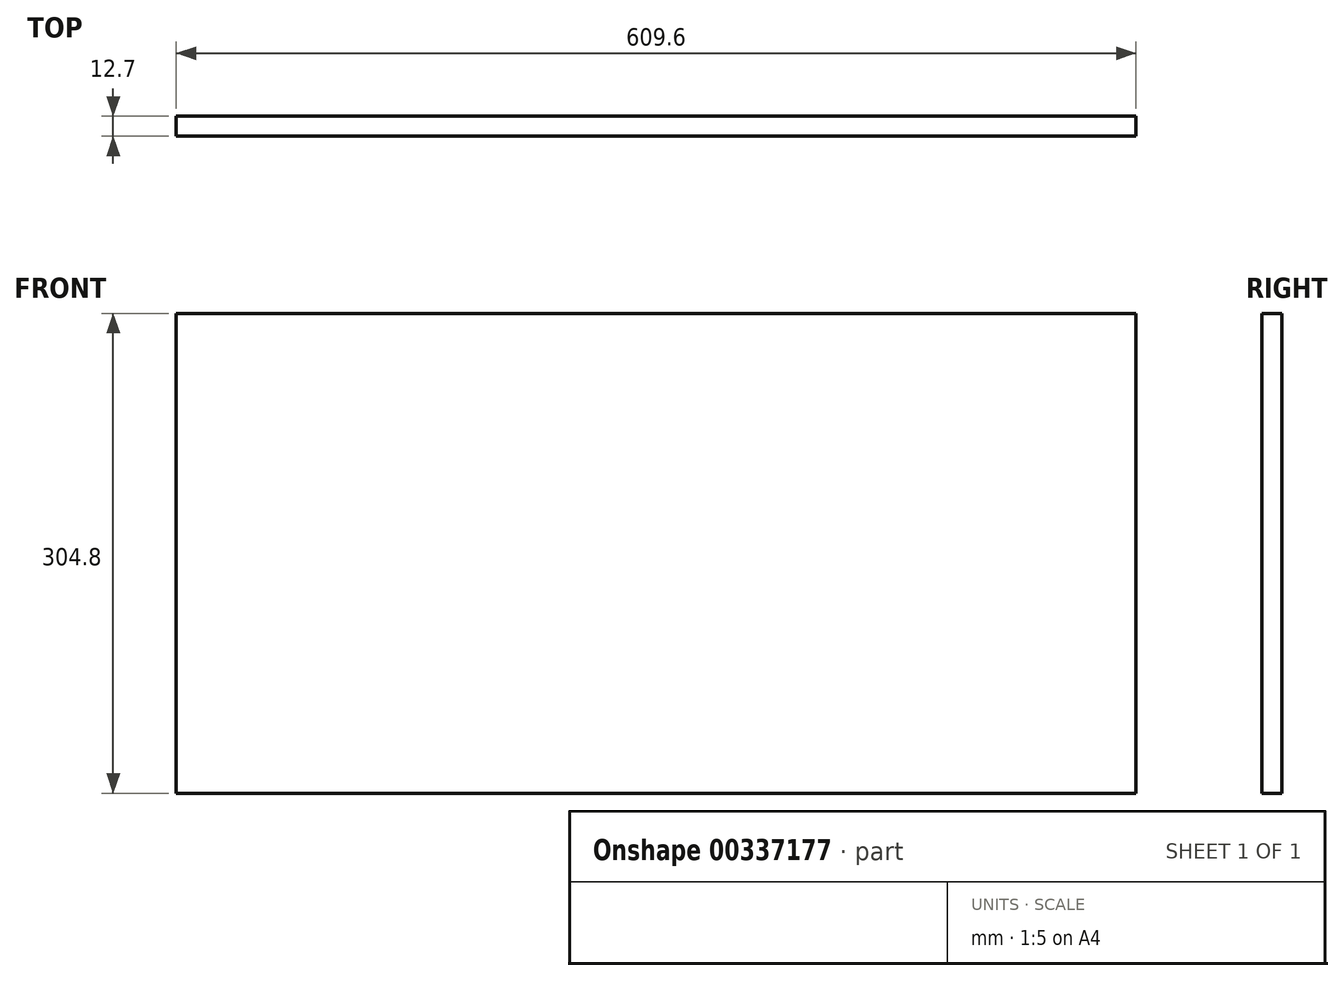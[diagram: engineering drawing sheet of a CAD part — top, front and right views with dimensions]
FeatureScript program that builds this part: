
annotation { "Feature Type Name" : "Feature", "Feature Type Description" : "" }
export const myFeature = defineFeature(function(context is Context, id is Id, definition is map)
    precondition{}
    {
        {
            var Q0;
            Q0=qCreatedBy(makeId("Front.planeOp"),FACE);
            var sketch = newSketch(context, id + "F0", { "sketchPlane" : qUnion([Q0])});
            skLineSegment(sketch, "E0.bottom", {"start": v(304.8, -152.4) * mm, "end": v(-304.8, -152.4) * mm});
            skLineSegment(sketch, "E0.top", {"start": v(304.8, 152.4) * mm, "end": v(-304.8, 152.4) * mm});
            skLineSegment(sketch, "E0.left", {"start": v(304.8, -152.4) * mm, "end": v(304.8, 152.4) * mm});
            skLineSegment(sketch, "E0.right", {"start": v(-304.8, -152.4) * mm, "end": v(-304.8, 152.4) * mm});
            skPoint(sketch, "E0.middle", {"position": v(0, 0) * mm});
            skSolve(sketch);
        }
        {
            var Q0;
            Q0 = qSketchRegion(id + "F0", true);
            extrude(context, id + "F1", {"entities" : qUnion([Q0]), "depth" : 12.7 * mm});
        }
    });
